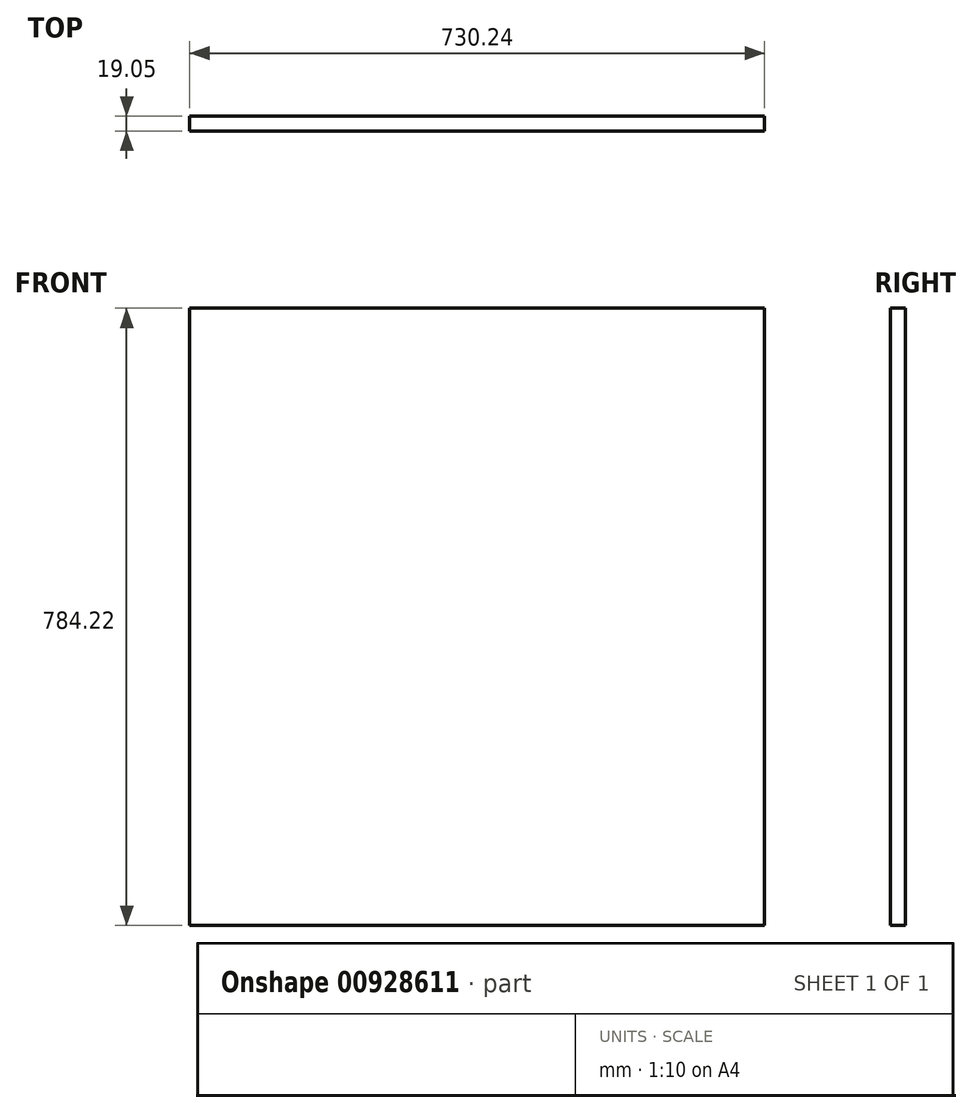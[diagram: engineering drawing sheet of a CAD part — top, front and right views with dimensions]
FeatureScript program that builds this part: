
annotation { "Feature Type Name" : "Feature", "Feature Type Description" : "" }
export const myFeature = defineFeature(function(context is Context, id is Id, definition is map)
    precondition{}
    {
        {
            var Q0;
            Q0=qCreatedBy(makeId("Front.planeOp"),FACE);
            var sketch = newSketch(context, id + "F0", { "sketchPlane" : qUnion([Q0])});
            skLineSegment(sketch, "E0.bottom", {"start": v(365.12, 392.11) * mm, "end": v(-365.13, 392.11) * mm});
            skLineSegment(sketch, "E0.top", {"start": v(365.12, -392.11) * mm, "end": v(-365.13, -392.11) * mm});
            skLineSegment(sketch, "E0.left", {"start": v(365.13, 392.11) * mm, "end": v(365.12, -392.11) * mm});
            skLineSegment(sketch, "E0.right", {"start": v(-365.13, 392.11) * mm, "end": v(-365.13, -392.11) * mm});
            skPoint(sketch, "E0.middle", {"position": v(0, 0) * mm});
            skSolve(sketch);
        }
        {
            var Q0;
            Q0=makeQuery(id+"F0.imprint","IMPRINT",FACE,{"disambiguationData":[TD([[makeQuery(id+"F0.imprint","IMPRINT",EDGE,{"derivedFrom":sQuery(id+"F0.wireOp",EDGE,"E0.bottom")}),1.0]])]});
            extrude(context, id + "F1", {"entities" : qUnion([Q0]), "depth" : 19.05 * mm, "offsetDistance" : 25.4 * mm});
        }
    });
